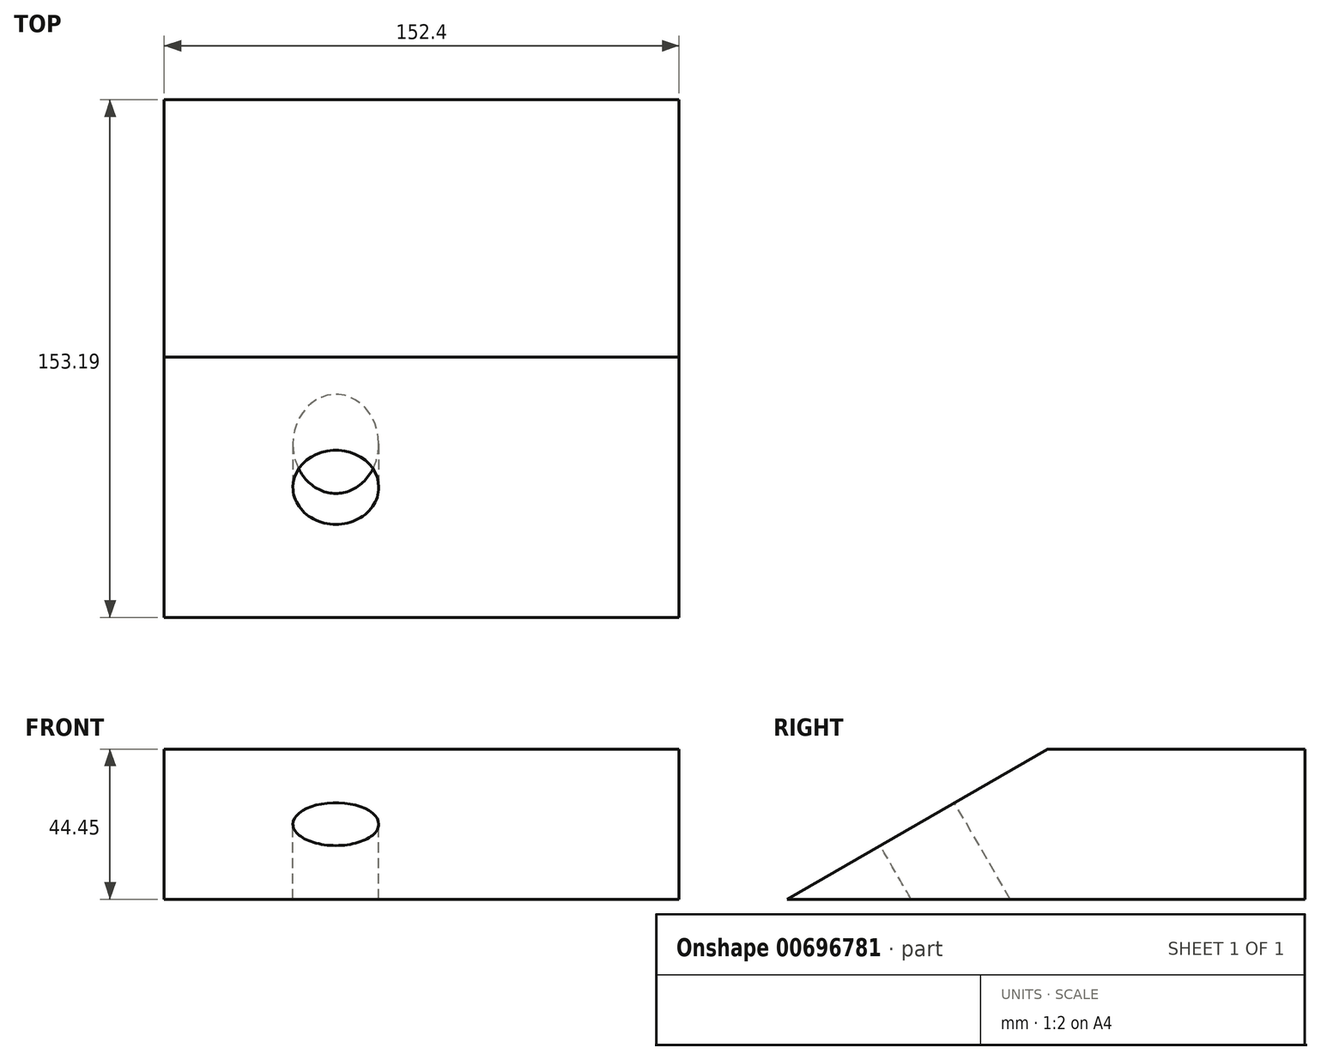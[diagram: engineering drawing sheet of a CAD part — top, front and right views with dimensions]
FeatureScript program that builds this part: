
annotation { "Feature Type Name" : "Feature", "Feature Type Description" : "" }
export const myFeature = defineFeature(function(context is Context, id is Id, definition is map)
    precondition{}
    {
        {
            var Q0;
            Q0=qCreatedBy(makeId("Right.planeOp"),FACE);
            var sketch = newSketch(context, id + "F0", { "sketchPlane" : qUnion([Q0])});
            skLineSegment(sketch, "E0", {"start": v(0, 0) * mm, "end": v(153.19, 0) * mm});
            skLineSegment(sketch, "E1", {"start": v(153.19, 0) * mm, "end": v(153.19, 44.45) * mm});
            skLineSegment(sketch, "E2", {"start": v(153.19, 44.45) * mm, "end": v(76.99, 44.45) * mm});
            skLineSegment(sketch, "E3", {"start": v(76.99, 44.45) * mm, "end": v(0, 0) * mm});
            skSolve(sketch);
        }
        {
            var Q0;
            Q0=makeQuery(id+"F0.imprint","IMPRINT",FACE,{"disambiguationData":[TD([[makeQuery(id+"F0.imprint","IMPRINT",EDGE,{"derivedFrom":sQuery(id+"F0.wireOp",EDGE,"E0")}),1.0]])]});
            extrude(context, id + "F1", {"entities" : qUnion([Q0]), "depth" : 152.4 * mm, "offsetDistance" : 25.4 * mm});
        }
        {
            var Q0;
            Q0=makeQuery(id+"F1.opExtrude","SWEPT_FACE",FACE,{"disambiguationData":[OSD([sQuery(id+"F0.wireOp",EDGE,"E3")])]});
            var sketch = newSketch(context, id + "F2", { "sketchPlane" : qUnion([Q0])});
            skCircle(sketch, "E4", {"center": v(50.8, 44.45) * mm, "radius": 12.7 * mm});
            skPoint(sketch, "E5", {"position": v(0, 44.45) * mm});
            skSolve(sketch);
        }
        {
            var Q0;
            Q0=makeQuery(id+"F2.imprint","IMPRINT",FACE,{"disambiguationData":[TD([[makeQuery(id+"F2.imprint","IMPRINT",EDGE,{"derivedFrom":sQuery(id+"F2.wireOp",EDGE,"E4")}),1.0]])]});
            extrude(context, id + "F3", {"entities" : qUnion([Q0]), "operationType" : NewBodyOperationType.REMOVE, "endBound" : BoundingType.UP_TO_NEXT, "oppositeDirection" : true, "depth" : 25.4 * mm, "offsetDistance" : 25.4 * mm});
        }
    });
